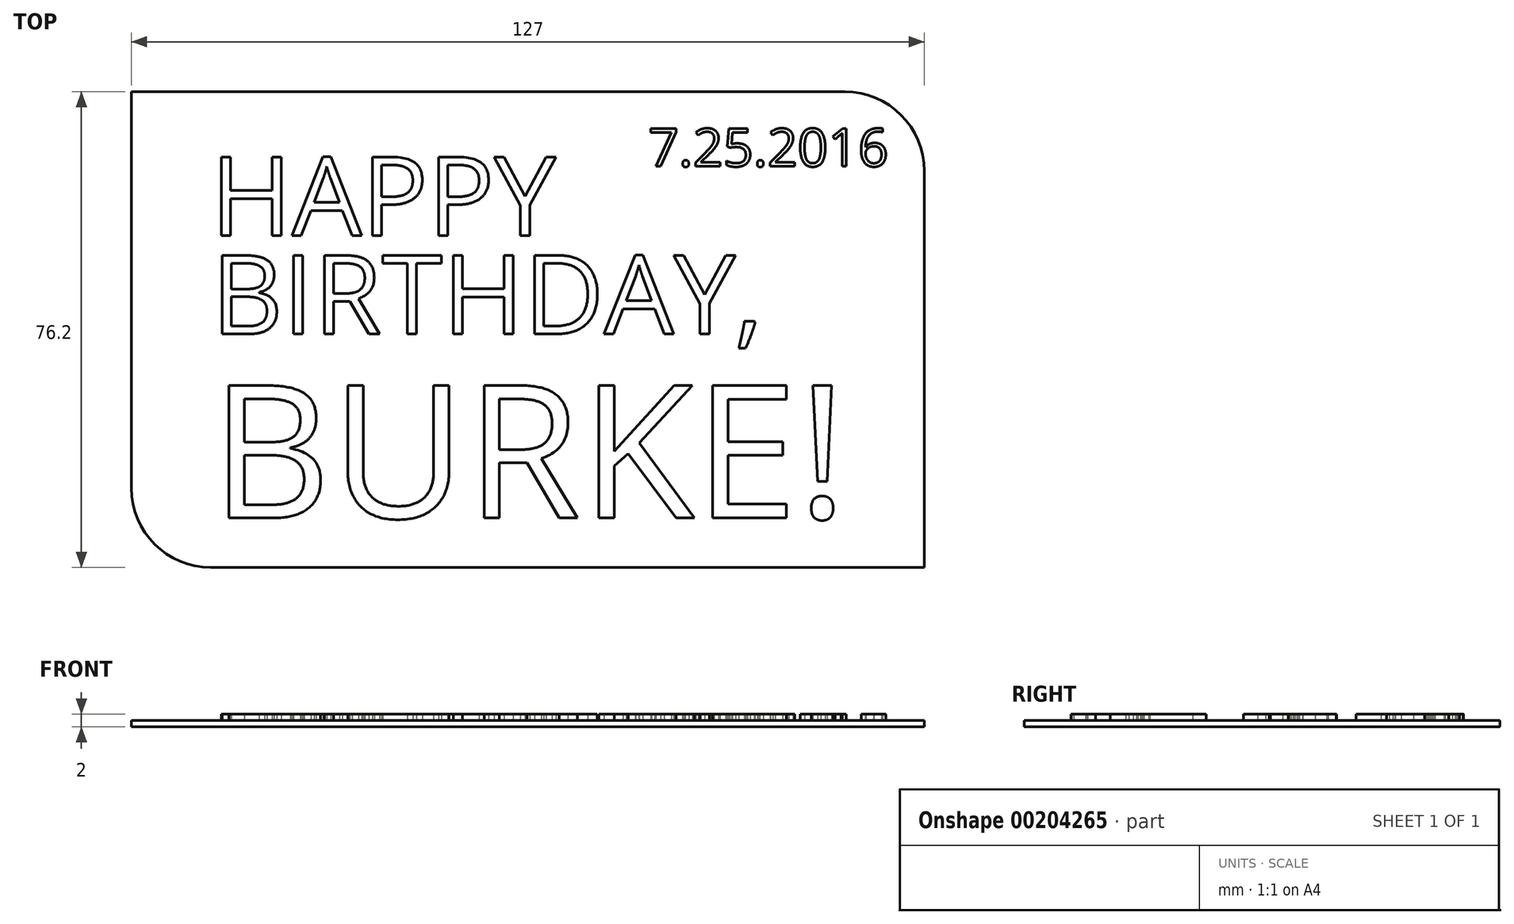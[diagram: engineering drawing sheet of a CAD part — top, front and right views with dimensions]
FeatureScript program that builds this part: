
annotation { "Feature Type Name" : "Feature", "Feature Type Description" : "" }
export const myFeature = defineFeature(function(context is Context, id is Id, definition is map)
    precondition{}
    {
        {
            var Q0;
            Q0=qCreatedBy(makeId("Top.planeOp"),FACE);
            var sketch = newSketch(context, id + "F0", { "sketchPlane" : qUnion([Q0])});
            skLineSegment(sketch, "E0.bottom", {"start": v(0, 0) * mm, "end": v(127, 0) * mm});
            skLineSegment(sketch, "E0.top", {"start": v(0, 76.2) * mm, "end": v(127, 76.2) * mm});
            skLineSegment(sketch, "E0.left", {"start": v(0, 0) * mm, "end": v(0, 76.2) * mm});
            skLineSegment(sketch, "E0.right", {"start": v(127, 0) * mm, "end": v(127, 76.2) * mm});
            skSolve(sketch);
        }
        {
            var Q0;
            Q0 = qSketchRegion(id + "F0", true);
            extrude(context, id + "F1", {"entities" : qUnion([Q0]), "depth" : 1 * mm});
        }
        {
            var Q0;
            Q0=makeQuery(id+"F1.opExtrude","CAP_FACE",FACE,{"disambiguationData":[OSD([sQuery(id+"F0.wireOp",EDGE,"E0.bottom"),sQuery(id+"F0.wireOp",EDGE,"E0.top"),sQuery(id+"F0.wireOp",EDGE,"E0.left"),sQuery(id+"F0.wireOp",EDGE,"E0.right")])],"isStart":false});
            var sketch = newSketch(context, id + "F2", { "sketchPlane" : qUnion([Q0])});
            skText(sketch, "E1", { "text": "HAPPY", "fontName": "OpenSans-Regular.ttf"});
            skText(sketch, "E2", { "text": "BIRTHDAY,", "fontName": "OpenSans-Regular.ttf"});
            skText(sketch, "E3", { "text": "BURKE!", "fontName": "OpenSans-Regular.ttf"});
            skLineSegment(sketch, "E4", {"start": v(63.5, 0) * mm, "end": v(63.5, 7.94) * mm, "construction": true});
            skText(sketch, "E5", { "text": "7.25.2016", "fontName": "OpenSans-Regular.ttf"});
            const initialGuessF2  = {"E1": [0.0127, 0.05315, 1, 0, 0.0127], "E2": [0.01283, 0.0374, 1, 0, 0.0127], "E3": [0.0127, 0.00794, 1, 0, 0.02139], "E5": [0.08282, 0.06424, 1, 0, 0.0061]};
            skSetInitialGuess(sketch, initialGuessF2);
            skSolve(sketch);
        }
        {
            var Q0;
            Q0 = qSketchRegion(id + "F2", true);
            extrude(context, id + "F3", {"entities" : qUnion([Q0]), "operationType" : NewBodyOperationType.ADD, "depth" : 1 * mm});
        }
        {
            var Q0;
            Q0=makeQuery(id+"F1.opExtrude","SWEPT_EDGE",EDGE,{"disambiguationData":[OSD([sQuery(id+"F0.wireOp",EDGE,"E0.bottom"),sQuery(id+"F0.wireOp",EDGE,"E0.left")])]});
            var Q1;
            Q1=makeQuery(id+"F1.opExtrude","SWEPT_EDGE",EDGE,{"disambiguationData":[OSD([sQuery(id+"F0.wireOp",EDGE,"E0.top"),sQuery(id+"F0.wireOp",EDGE,"E0.right")])]});
            fillet(context, id + "F4", {"entities" : qUnion([Q0, Q1]), "radius" : 12.7 * mm, "tangentPropagation" : true, "allowEdgeOverflow" : false});
        }
    });
